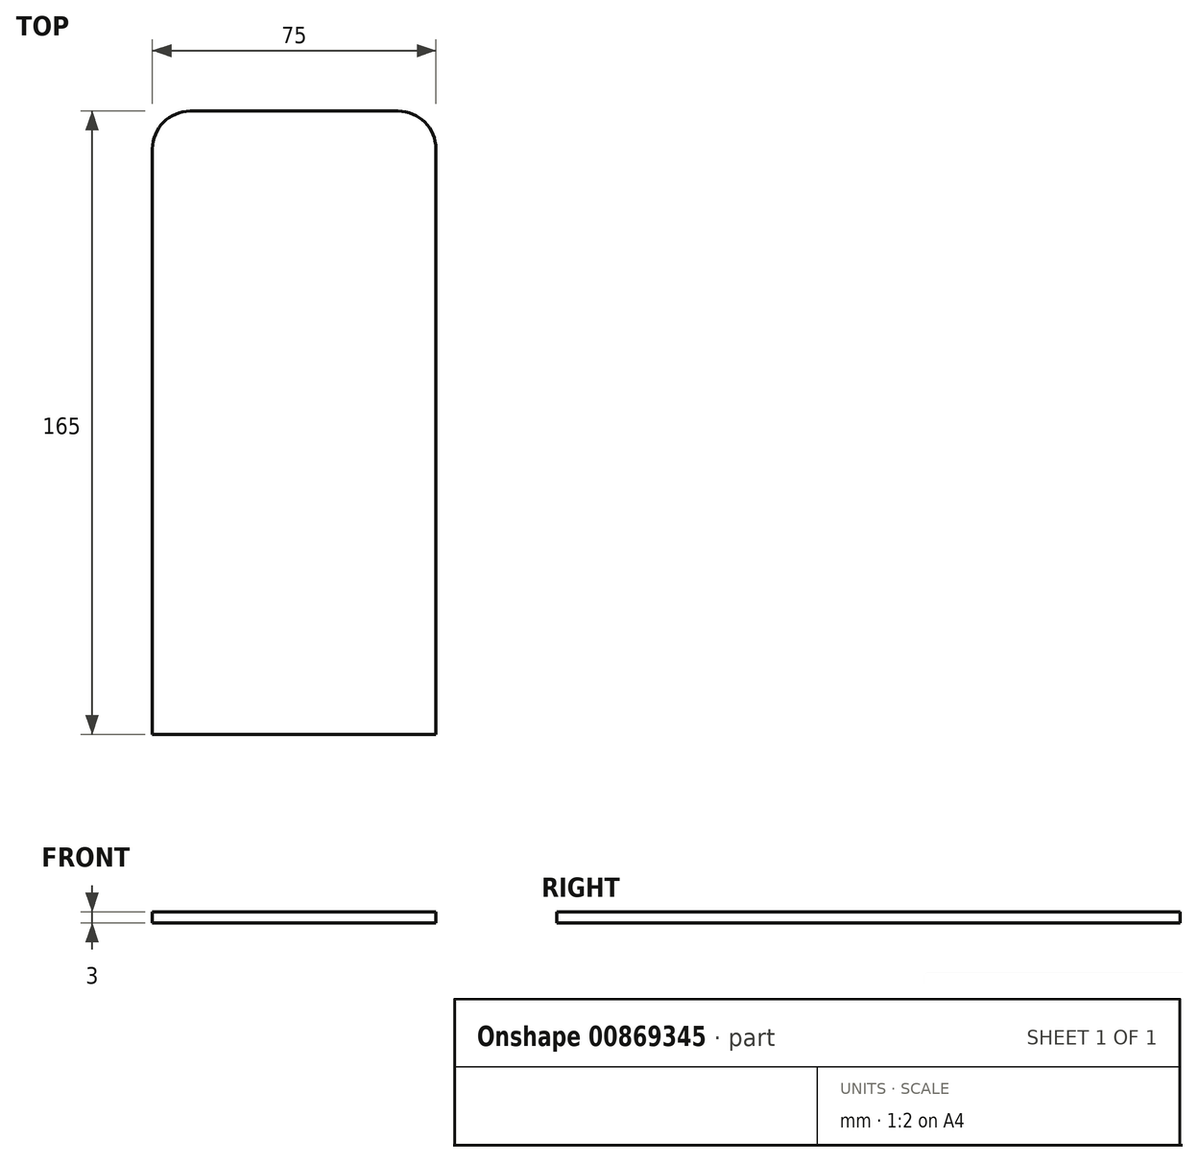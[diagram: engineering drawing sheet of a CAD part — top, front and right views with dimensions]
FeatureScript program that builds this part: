
annotation { "Feature Type Name" : "Feature", "Feature Type Description" : "" }
export const myFeature = defineFeature(function(context is Context, id is Id, definition is map)
    precondition{}
    {
        {
            var Q0;
            Q0=qCreatedBy(makeId("Top.planeOp"),FACE);
            var sketch = newSketch(context, id + "F0", { "sketchPlane" : qUnion([Q0])});
            skLineSegment(sketch, "E0.bottom", {"start": v(27.5, 82.5) * mm, "end": v(-27.5, 82.5) * mm});
            skLineSegment(sketch, "E0.top", {"start": v(37.5, -82.5) * mm, "end": v(-37.5, -82.5) * mm});
            skLineSegment(sketch, "E0.left", {"start": v(37.5, 72.5) * mm, "end": v(37.5, -82.5) * mm});
            skLineSegment(sketch, "E0.right", {"start": v(-37.5, 72.5) * mm, "end": v(-37.5, -82.5) * mm});
            skPoint(sketch, "E0.middle", {"position": v(0, 0) * mm});
            skPoint(sketch, "E1.visualSharp", {"position": v(-37.5, 82.5) * mm});
            skArc(sketch, "E1.filletArc", {"start": v(-27.5, 82.5) * mm, "mid": v(-34.57, 79.57) * mm, "end": v(-37.5, 72.5) * mm});
            skPoint(sketch, "E2.visualSharp", {"position": v(37.5, 82.5) * mm});
            skArc(sketch, "E2.filletArc", {"start": v(37.5, 72.5) * mm, "mid": v(34.57, 79.57) * mm, "end": v(27.5, 82.5) * mm});
            skSolve(sketch);
        }
        {
            var Q0;
            Q0 = qSketchRegion(id + "F0", true);
            extrude(context, id + "F1", {"entities" : qUnion([Q0]), "depth" : 3 * mm, "offsetDistance" : 25 * mm});
        }
    });
